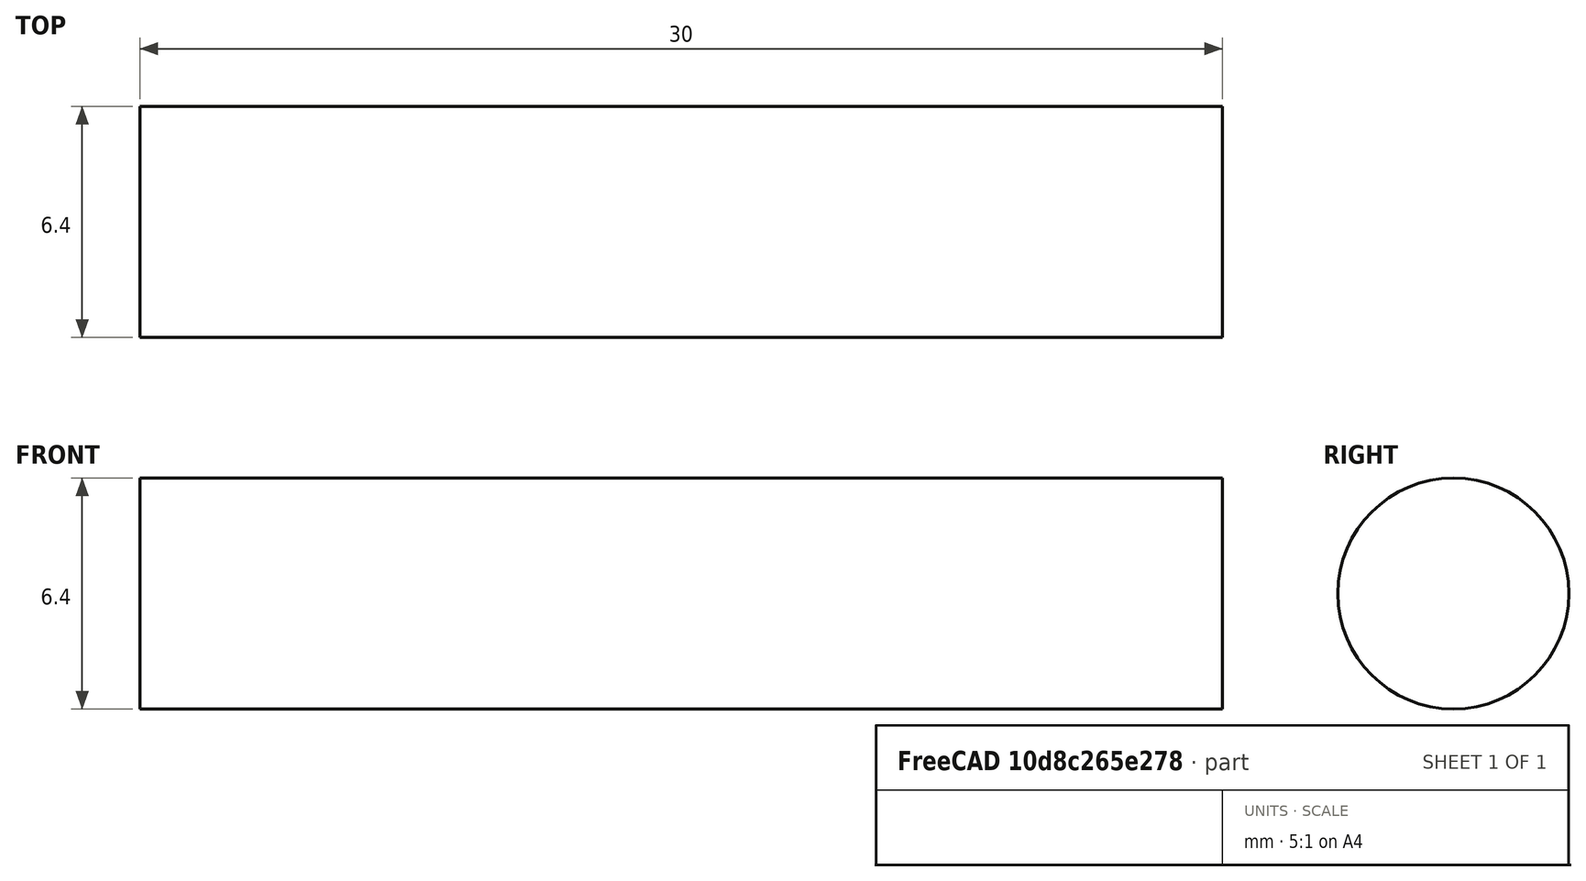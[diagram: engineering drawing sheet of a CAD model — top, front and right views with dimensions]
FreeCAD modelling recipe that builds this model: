
FCSTD DOCUMENT  (FreeCAD 0.19R)
Label: E8_D6_4_stub
License: All rights reserved
LicenseURL: http://en.wikipedia.org/wiki/All_rights_reserved
objects: Sketcher::SketchObject×1, PartDesign::Revolution×1, PartDesign::Body×1
note: 4 computed .brp shape members not serialized (recipe doc carries the construction recipe); baked Part::Feature solids carry a one-line shape summary decoded from their .brp

FEATURE [Sketcher::SketchObject] Sketch
  FullyConstrained = false
  MapMode = 5
  Support = -> [XY_Plane]
  sketch-geometry (7):
    g0: GeomPoint X=0 Y=3.2 Z=0
    g1: GeomPoint X=30 Y=3.2 Z=0
    g2: GeomPoint X=92.5486 Y=36.3931 Z=0
    g3: LineSegment StartX=0 StartY=0 StartZ=0 EndX=0 EndY=3.2 EndZ=0
    g4: LineSegment StartX=0 StartY=3.2 StartZ=0 EndX=30 EndY=3.2 EndZ=0
    g5: LineSegment StartX=30 StartY=3.2 StartZ=0 EndX=30 EndY=0 EndZ=0
    g6: LineSegment StartX=0 StartY=0 StartZ=0 EndX=30 EndY=0 EndZ=0
  constraints (12):
    c: Coincident(g3,g-1)
    c: Coincident(g3,g0)
    c: Vertical(g3)
    c: Coincident(g4,g3)
    c: Horizontal(g4)
    c: DistanceX(g4,g4) = 30
    c: Coincident(g5,g4)
    c: Vertical(g5)
    c: Coincident(g6,g3)
    c: Coincident(g6,g5)
    c: DistanceY(g3,g3) = 3.2
    c: Parallel(g4,g6)
FEATURE [PartDesign::Revolution] Revolution
  Angle = 360
  Axis = (1,0,0)
  Base = (0,0,0)
  Profile = -> Sketch
  ReferenceAxis = -> Sketch [H_Axis]
FEATURE [PartDesign::Body] Body
  Group = -> [Sketch,Revolution]
  Origin = -> Origin
  Tip = -> Revolution
